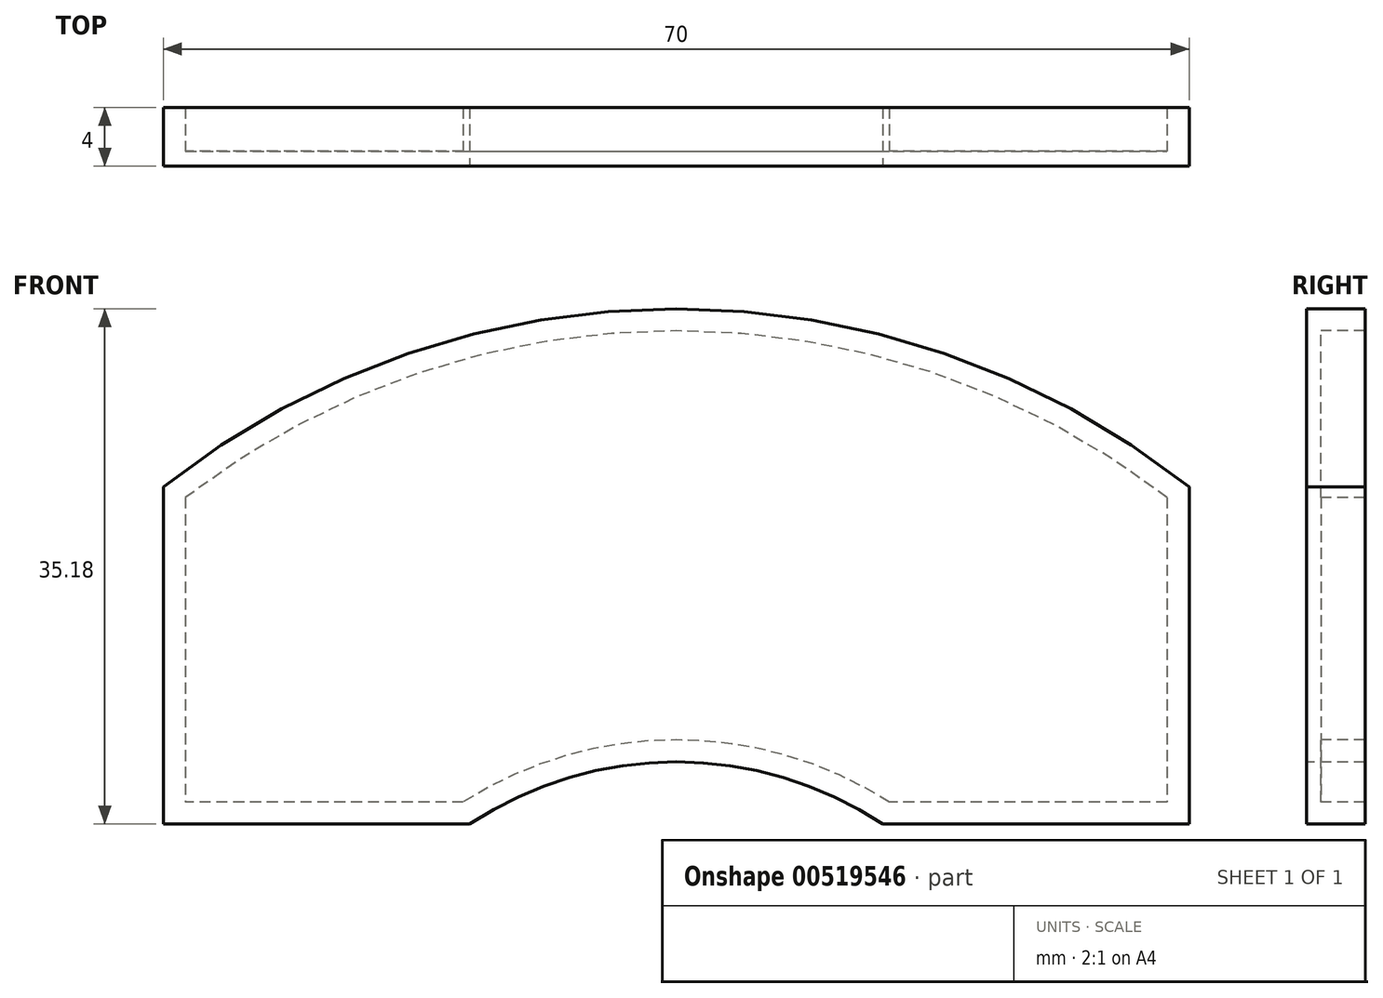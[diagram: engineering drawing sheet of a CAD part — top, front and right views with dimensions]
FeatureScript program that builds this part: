
annotation { "Feature Type Name" : "Feature", "Feature Type Description" : "" }
export const myFeature = defineFeature(function(context is Context, id is Id, definition is map)
    precondition{}
    {
        {
            var Q0;
            Q0=qCreatedBy(makeId("Front.planeOp"),FACE);
            var sketch = newSketch(context, id + "F0", { "sketchPlane" : qUnion([Q0])});
            skLineSegment(sketch, "E0.top", {"start": v(35, 21.31) * mm, "end": v(14.1, 21.31) * mm});
            skLineSegment(sketch, "E0.left", {"start": v(35, 44.34) * mm, "end": v(35, 21.31) * mm});
            skLineSegment(sketch, "E0.right", {"start": v(-35, 44.34) * mm, "end": v(-35, 21.31) * mm});
            skArc(sketch, "E1", {"start": v(35, 44.34) * mm, "mid": v(0, 56.49) * mm, "end": v(-35, 44.34) * mm});
            skPoint(sketch, "E2.orphan", {"position": v(35, 60.8) * mm});
            skPoint(sketch, "E3.orphan", {"position": v(-35, 60.8) * mm});
            skArc(sketch, "E4", {"start": v(14.1, 21.31) * mm, "mid": v(0, 25.55) * mm, "end": v(-14.1, 21.31) * mm});
            skLineSegment(sketch, "E5.trimOffspring", {"start": v(-14.1, 21.31) * mm, "end": v(-35, 21.31) * mm});
            skSolve(sketch);
        }
        {
            var Q0;
            Q0=makeQuery(id+"F0.imprint","IMPRINT",FACE,{"disambiguationData":[TD([[makeQuery(id+"F0.imprint","IMPRINT",EDGE,{"derivedFrom":sQuery(id+"F0.wireOp",EDGE,"E0.top")}),-1.0]])]});
            extrude(context, id + "F1", {"entities" : qUnion([Q0]), "oppositeDirection" : true, "depth" : 1 * mm, "offsetDistance" : 25 * mm});
        }
        {
            var Q0;
            Q0=makeQuery(id+"F1.opExtrude","CAP_FACE",FACE,{"disambiguationData":[OSD([sQuery(id+"F0.wireOp",EDGE,"E0.top"),sQuery(id+"F0.wireOp",EDGE,"E0.left"),sQuery(id+"F0.wireOp",EDGE,"E0.right"),sQuery(id+"F0.wireOp",EDGE,"E1"),sQuery(id+"F0.wireOp",EDGE,"E4"),sQuery(id+"F0.wireOp",EDGE,"E5.trimOffspring")])],"isStart":false});
            var sketch = newSketch(context, id + "F2", { "sketchPlane" : qUnion([Q0])});
            skArc(sketch, "E6.0", {"start": v(-33.5, 43.6) * mm, "mid": v(0, 54.99) * mm, "end": v(33.5, 43.6) * mm});
            skLineSegment(sketch, "E7.0", {"start": v(-33.5, 43.6) * mm, "end": v(-33.5, 22.81) * mm});
            skLineSegment(sketch, "E8.0", {"start": v(-33.5, 22.81) * mm, "end": v(-14.53, 22.81) * mm});
            skArc(sketch, "E9.0", {"start": v(-14.53, 22.81) * mm, "mid": v(0, 27.05) * mm, "end": v(14.53, 22.81) * mm});
            skLineSegment(sketch, "E10.0", {"start": v(14.53, 22.81) * mm, "end": v(33.5, 22.81) * mm});
            skLineSegment(sketch, "E11.0", {"start": v(33.5, 43.6) * mm, "end": v(33.5, 22.81) * mm});
            skSolve(sketch);
        }
        {
            var Q0;
            Q0=makeQuery(id+"F2.imprint","IMPRINT",FACE,{"disambiguationData":[TD([[makeQuery(id+"F2.imprint","IMPRINT",EDGE,{"derivedFrom":sQuery(id+"F2.wireOp",EDGE,"E6.0")}),-1.0]])]});
            extrude(context, id + "F3", {"entities" : qUnion([Q0]), "operationType" : NewBodyOperationType.ADD, "depth" : 3 * mm, "offsetDistance" : 25 * mm});
        }
    });
